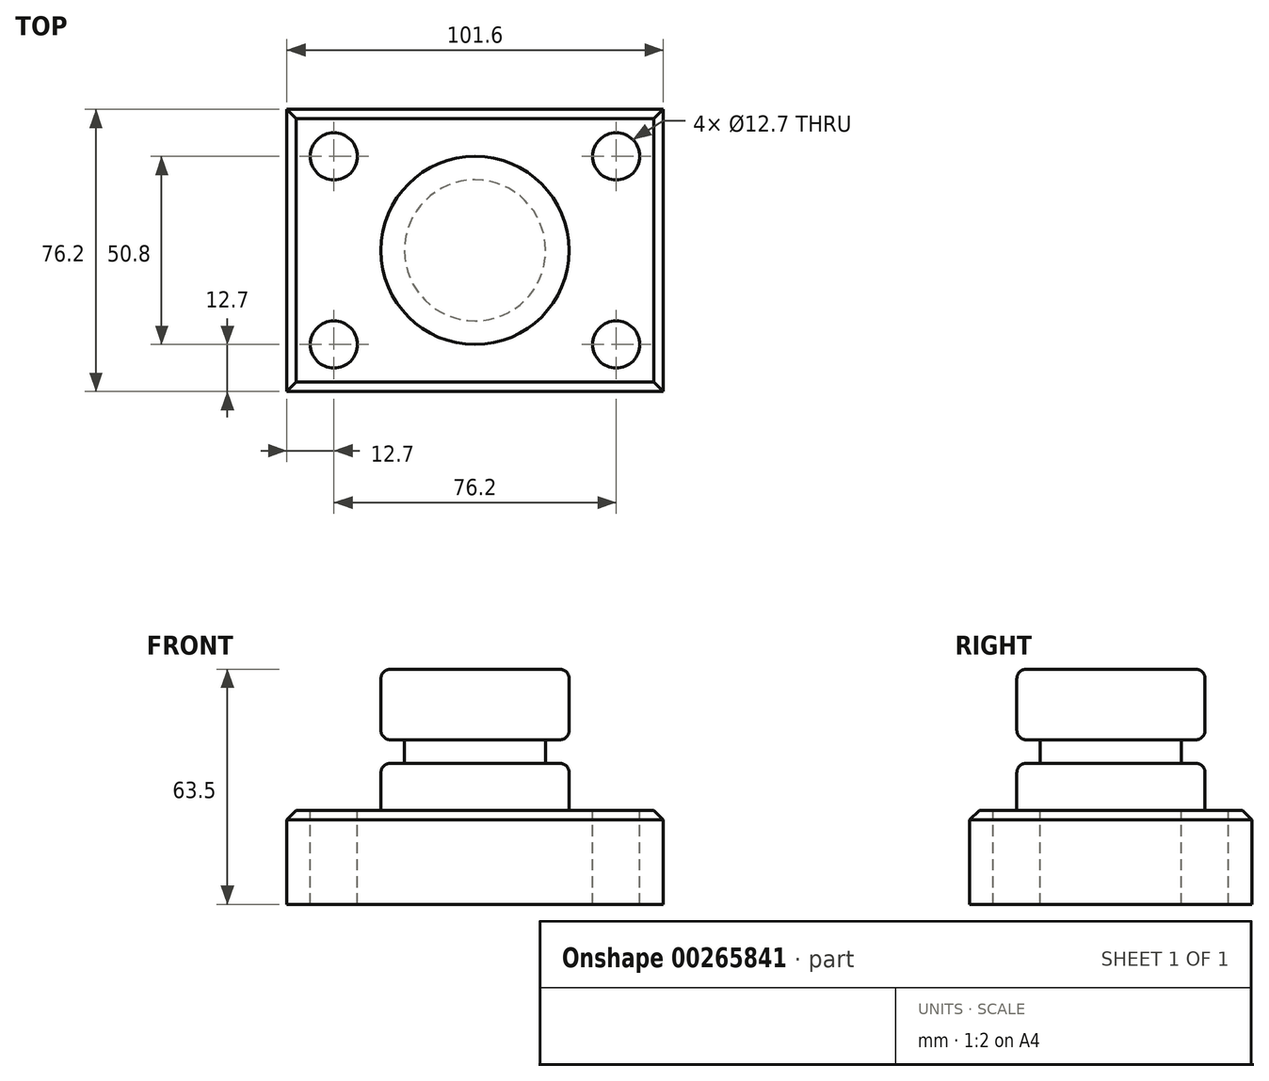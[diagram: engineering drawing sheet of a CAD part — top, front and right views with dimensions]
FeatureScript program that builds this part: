
annotation { "Feature Type Name" : "Feature", "Feature Type Description" : "" }
export const myFeature = defineFeature(function(context is Context, id is Id, definition is map)
    precondition{}
    {
        {
            var Q0;
            Q0=qCreatedBy(makeId("Top.planeOp"),FACE);
            var sketch = newSketch(context, id + "F0", { "sketchPlane" : qUnion([Q0])});
            skLineSegment(sketch, "E0.bottom", {"start": v(-50.8, 38.1) * mm, "end": v(50.8, 38.1) * mm});
            skLineSegment(sketch, "E0.top", {"start": v(-50.8, -38.1) * mm, "end": v(50.8, -38.1) * mm});
            skLineSegment(sketch, "E0.left", {"start": v(-50.8, 38.1) * mm, "end": v(-50.8, -38.1) * mm});
            skLineSegment(sketch, "E0.right", {"start": v(50.8, 38.1) * mm, "end": v(50.8, -38.1) * mm});
            skSolve(sketch);
        }
        {
            var Q0;
            Q0=makeQuery(id+"F0.imprint","IMPRINT",FACE,{"disambiguationData":[TD([[makeQuery(id+"F0.imprint","IMPRINT",EDGE,{"derivedFrom":sQuery(id+"F0.wireOp",EDGE,"E0.bottom")}),-1.0]])]});
            extrude(context, id + "F1", {"entities" : qUnion([Q0]), "oppositeDirection" : true, "depth" : 25.4 * mm});
        }
        {
            var Q0;
            Q0=makeQuery(id+"F1.opExtrude","CAP_FACE",FACE,{"disambiguationData":[OSD([sQuery(id+"F0.wireOp",EDGE,"E0.bottom"),sQuery(id+"F0.wireOp",EDGE,"E0.top"),sQuery(id+"F0.wireOp",EDGE,"E0.left"),sQuery(id+"F0.wireOp",EDGE,"E0.right")])],"isStart":true});
            var sketch = newSketch(context, id + "F2", { "sketchPlane" : qUnion([Q0])});
            skCircle(sketch, "E1", {"center": v(38.1, -25.4) * mm, "radius": 6.35 * mm});
            skCircle(sketch, "E2", {"center": v(38.1, 25.4) * mm, "radius": 6.35 * mm});
            skCircle(sketch, "E3", {"center": v(-38.1, 25.4) * mm, "radius": 6.35 * mm});
            skCircle(sketch, "E4", {"center": v(-38.1, -25.4) * mm, "radius": 6.35 * mm});
            skSolve(sketch);
        }
        {
            var Q0;
            Q0=makeQuery(id+"F2.imprint","IMPRINT",FACE,{"disambiguationData":[TD([[makeQuery(id+"F2.imprint","IMPRINT",EDGE,{"derivedFrom":sQuery(id+"F2.wireOp",EDGE,"E1")}),1.0]])]});
            var Q1;
            Q1=makeQuery(id+"F2.imprint","IMPRINT",FACE,{"disambiguationData":[TD([[makeQuery(id+"F2.imprint","IMPRINT",EDGE,{"derivedFrom":sQuery(id+"F2.wireOp",EDGE,"E2")}),1.0]])]});
            var Q2;
            Q2=makeQuery(id+"F2.imprint","IMPRINT",FACE,{"disambiguationData":[TD([[makeQuery(id+"F2.imprint","IMPRINT",EDGE,{"derivedFrom":sQuery(id+"F2.wireOp",EDGE,"E3")}),1.0]])]});
            var Q3;
            Q3=makeQuery(id+"F2.imprint","IMPRINT",FACE,{"disambiguationData":[TD([[makeQuery(id+"F2.imprint","IMPRINT",EDGE,{"derivedFrom":sQuery(id+"F2.wireOp",EDGE,"E4")}),1.0]])]});
            extrude(context, id + "F3", {"entities" : qUnion([Q0, Q1, Q2, Q3]), "operationType" : NewBodyOperationType.REMOVE, "oppositeDirection" : true, "depth" : 25.4 * mm});
        }
        {
            var Q0;
            Q0=qCreatedBy(makeId("Front.planeOp"),FACE);
            var sketch = newSketch(context, id + "F4", { "sketchPlane" : qUnion([Q0])});
            skLineSegment(sketch, "E5.bottom", {"start": v(-25.4, 38.1) * mm, "end": v(0, 38.1) * mm});
            skLineSegment(sketch, "E5.top", {"start": v(-25.4, 0) * mm, "end": v(0, 0) * mm});
            skLineSegment(sketch, "E5.left", {"start": v(-25.4, 38.1) * mm, "end": v(-25.4, 0) * mm});
            skLineSegment(sketch, "E5.right", {"start": v(0, 38.1) * mm, "end": v(0, 0) * mm});
            skSolve(sketch);
        }
        {
            var Q0;
            Q0=makeQuery(id+"F4.imprint","IMPRINT",FACE,{"disambiguationData":[TD([[makeQuery(id+"F4.imprint","IMPRINT",EDGE,{"derivedFrom":sQuery(id+"F4.wireOp",EDGE,"E5.bottom")}),-1.0]])]});
            var Q1;
            Q1=sQuery(id+"F4.wireOp",EDGE,"E5.right");
            revolve(context, id + "F5", {"operationType" : NewBodyOperationType.ADD, "entities" : qUnion([Q0]), "axis" : qUnion([Q1]), "revolveType" : RevolveType.FULL});
        }
        {
            var Q0;
            Q0=qCreatedBy(makeId("Right.planeOp"),FACE);
            var sketch = newSketch(context, id + "F6", { "sketchPlane" : qUnion([Q0])});
            skLineSegment(sketch, "E6.bottom", {"start": v(0, 0) * mm, "end": v(-19.05, 0) * mm});
            skLineSegment(sketch, "E6.top", {"start": v(0, 12.7) * mm, "end": v(-19.05, 12.7) * mm});
            skLineSegment(sketch, "E6.left", {"start": v(0, 0) * mm, "end": v(0, 12.7) * mm});
            skLineSegment(sketch, "E6.right", {"start": v(-19.05, 0) * mm, "end": v(-19.05, 12.7) * mm});
            skLineSegment(sketch, "E7.bottom", {"start": v(-19.05, 12.7) * mm, "end": v(-46.35, 12.7) * mm});
            skLineSegment(sketch, "E7.top", {"start": v(-19.05, 19.05) * mm, "end": v(-46.35, 19.05) * mm});
            skLineSegment(sketch, "E7.left", {"start": v(-19.05, 12.7) * mm, "end": v(-19.05, 19.05) * mm});
            skLineSegment(sketch, "E7.right", {"start": v(-46.35, 12.7) * mm, "end": v(-46.35, 19.05) * mm});
            skSolve(sketch);
        }
        {
            var Q0;
            Q0=makeQuery(id+"F6.imprint","IMPRINT",FACE,{"disambiguationData":[TD([[makeQuery(id+"F6.imprint","IMPRINT",EDGE,{"derivedFrom":sQuery(id+"F6.wireOp",EDGE,"E7.bottom")}),-1.0]])]});
            var Q1;
            Q1=sQuery(id+"F6.wireOp",EDGE,"E6.left");
            revolve(context, id + "F7", {"operationType" : NewBodyOperationType.REMOVE, "entities" : qUnion([Q0]), "axis" : qUnion([Q1]), "revolveType" : RevolveType.FULL, "oppositeDirection" : true});
        }
        {
            var Q0;
            Q0=makeQuery(id+"F1.opExtrude","CAP_EDGE",EDGE,{"disambiguationData":[OSD([sQuery(id+"F0.wireOp",EDGE,"E0.right")])],"isStart":true});
            var Q1;
            Q1=makeQuery(id+"F1.opExtrude","CAP_EDGE",EDGE,{"disambiguationData":[OSD([sQuery(id+"F0.wireOp",EDGE,"E0.top")])],"isStart":true});
            var Q2;
            Q2=makeQuery(id+"F1.opExtrude","CAP_EDGE",EDGE,{"disambiguationData":[OSD([sQuery(id+"F0.wireOp",EDGE,"E0.bottom")])],"isStart":true});
            var Q3;
            Q3=makeQuery(id+"F1.opExtrude","CAP_EDGE",EDGE,{"disambiguationData":[OSD([sQuery(id+"F0.wireOp",EDGE,"E0.left")])],"isStart":true});
            chamfer(context, id + "F8", {"entities" : qUnion([Q0, Q1, Q2, Q3]), "width" : 2.54 * mm, "tangentPropagation" : true});
        }
        {
            var Q0;
            Q0=makeQuery(id+"F5.opRevolve","SWEPT_EDGE",EDGE,{"disambiguationData":[OSD([sQuery(id+"F4.wireOp",EDGE,"E5.top"),sQuery(id+"F4.wireOp",EDGE,"E5.left")])]});
            var Q1;
            Q1=makeQuery(id+"F7.boolean.opBoolean","INTERSECT",EDGE,{"derivedFrom":[makeQuery(id+"F5.opRevolve","SWEPT_FACE",FACE,{"disambiguationData":[OSD([sQuery(id+"F4.wireOp",EDGE,"E5.left")])]}),makeQuery(id+"F7.opRevolve","SWEPT_FACE",FACE,{"disambiguationData":[OSD([sQuery(id+"F6.wireOp",EDGE,"E7.bottom")])]})]});
            var Q2;
            Q2=makeQuery(id+"F7.boolean.opBoolean","SPLIT",FACE,{"disambiguationData":[TD([makeQuery(id+"F5.opRevolve","SWEPT_FACE",FACE,{"disambiguationData":[OSD([sQuery(id+"F4.wireOp",EDGE,"E5.bottom")])]})])],"derivedFrom":makeQuery(id+"F5.opRevolve","SWEPT_FACE",FACE,{"disambiguationData":[OSD([sQuery(id+"F4.wireOp",EDGE,"E5.left")])]})});
            fillet(context, id + "F9", {"entities" : qUnion([Q0, Q1, Q2]), "radius" : 2.54 * mm, "tangentPropagation" : true, "allowEdgeOverflow" : false});
        }
    });
